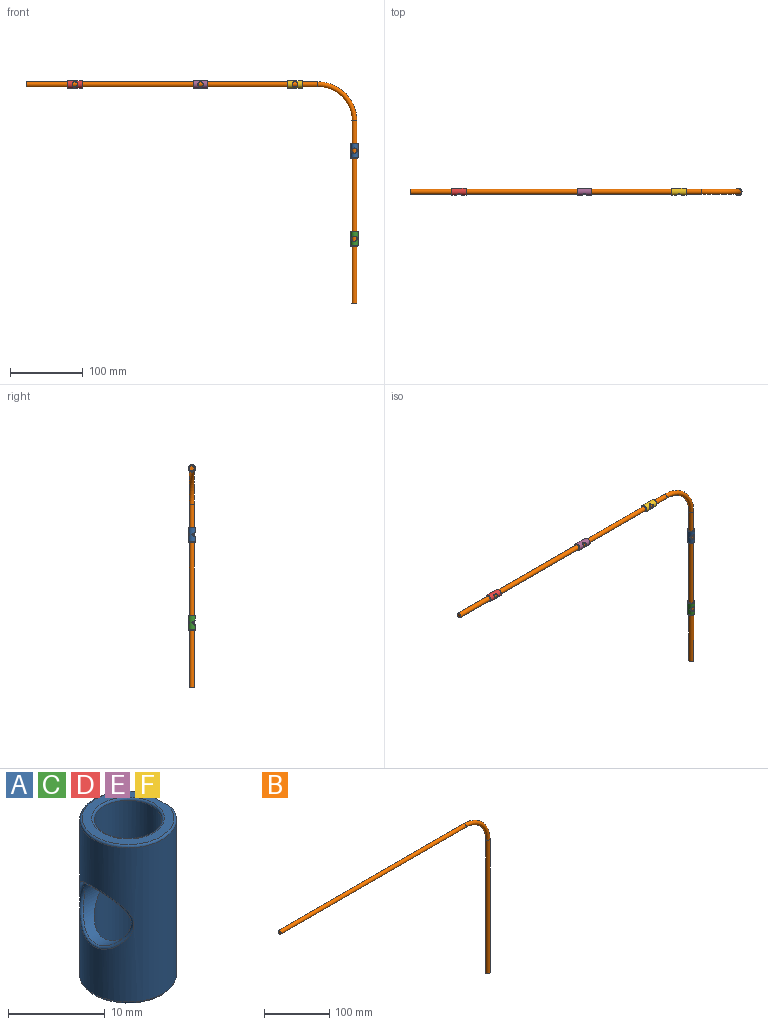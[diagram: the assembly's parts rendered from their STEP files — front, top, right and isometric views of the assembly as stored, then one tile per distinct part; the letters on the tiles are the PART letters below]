
ASSEMBLY  parts=6 mates=5
PART A: 16 faces, bbox 10.7x11x20.2 mm
  f0: bspline ~2.07x0.65mm, area 0mm2, adj f1,f15
  f1: cone r=1.5mm half-angle=45deg, axis (-1,0,0), area 17.8mm2, adj f0,f2,f3,f14,f15
  f2: bspline ~2.07x0.64mm, area 0mm2, adj f1,f15
  f3: cylinder r=2.5mm len=5mm, axis (-1,0,0), area 0mm2, adj f1,f4
  f4: cylinder r=3.5mm len=19.5mm, axis (0,0,-1), area 369.1mm2, adj f3,f5,f12,f13,f14
  f5: torus R=3.75mm, axis (0,0,-1), area 8.9mm2, adj f4,f6
  f6: plane 9.5x9.25mm, normal (0,0,-1), area 26.2mm2, adj f5,f7,f15
  f7: torus R=4.75mm, axis (0,0,-1), area 10.6mm2, adj f6,f8,f15
  f8: cylinder r=5mm len=19.5mm, axis (0,0,-1), area 473.2mm2, adj f7,f9,f10,f15
  f9: bspline ~7.9x7.5mm, area 12.1mm2, adj f8,f13
  f10: torus R=4.75mm, axis (0,0,-1), area 10.6mm2, adj f8,f11,f15
  f11: plane 9.5x9.25mm, normal (0,0,1), area 26.2mm2, adj f10,f12,f15
  f12: torus R=3.75mm, axis (0,0,-1), area 8.9mm2, adj f4,f11
  f13: cylinder r=3.5mm len=7mm, axis (1,0,0), area 36.5mm2, adj f4,f9
  f14: cylinder r=2.5mm len=5mm, axis (-1,0,0), area 0mm2, adj f1,f4
  f15: plane 20.17x4.53mm, normal (1,0,0), area 80mm2, adj f0,f1,f2,f6,f7,f8,f10,f11
PART B: 5 faces, bbox 457.8x6.8x307.8 mm
  f0: plane 6.8x6.8mm, normal (0,0,-1), area 36.3mm2, adj f2
  f1: plane 6.8x6.8mm, normal (-1,0,0), area 36.3mm2, adj f4
  f2: cylinder r=3.4mm len=250mm, axis (0,0,1), area 5340.7mm2, adj f0,f3
  f3: torus R=50mm, axis (0,-1,0), area 1677.8mm2, adj f2,f4
  f4: cylinder r=3.4mm len=400mm, axis (-1,0,0), area 8545.1mm2, adj f1,f3
PART C: same geometry as A
PART D: same geometry as A
PART E: same geometry as A
PART F: same geometry as A
PLACE A rot(axis=(0,0,1),90deg) t=(409.91,-15.94,146.99)mm
PLACE B t=(409.91,-15.94,-52.07)mm
PLACE C rot(axis=(0,0,1),90deg) t=(409.91,-15.94,26.32)mm
PLACE D rot(axis=(0.58,0.58,0.58),120deg) t=(16.98,-15.94,247.93)mm
PLACE E rot(axis=(0.58,0.58,0.58),120deg) t=(189.14,-15.94,247.93)mm
PLACE F rot(axis=(0.58,0.58,0.58),120deg) t=(318.51,-15.94,247.93)mm
MATE slider B.f4 <-> E.f4  axis (-1,0,0) through (-40.09,-15.94,247.93)mm
MATE slider B.f4 <-> D.f4  axis (-1,0,0) through (-40.09,-15.94,247.93)mm
MATE slider A.f4 <-> B.f2  axis (0,0,-1) through (409.91,-15.94,166.74)mm
MATE slider B.f4 <-> F.f4  axis (-1,0,0) through (-40.09,-15.94,247.93)mm
MATE slider C.f4 <-> B.f2  axis (0,0,1) through (409.91,-15.94,46.32)mm
